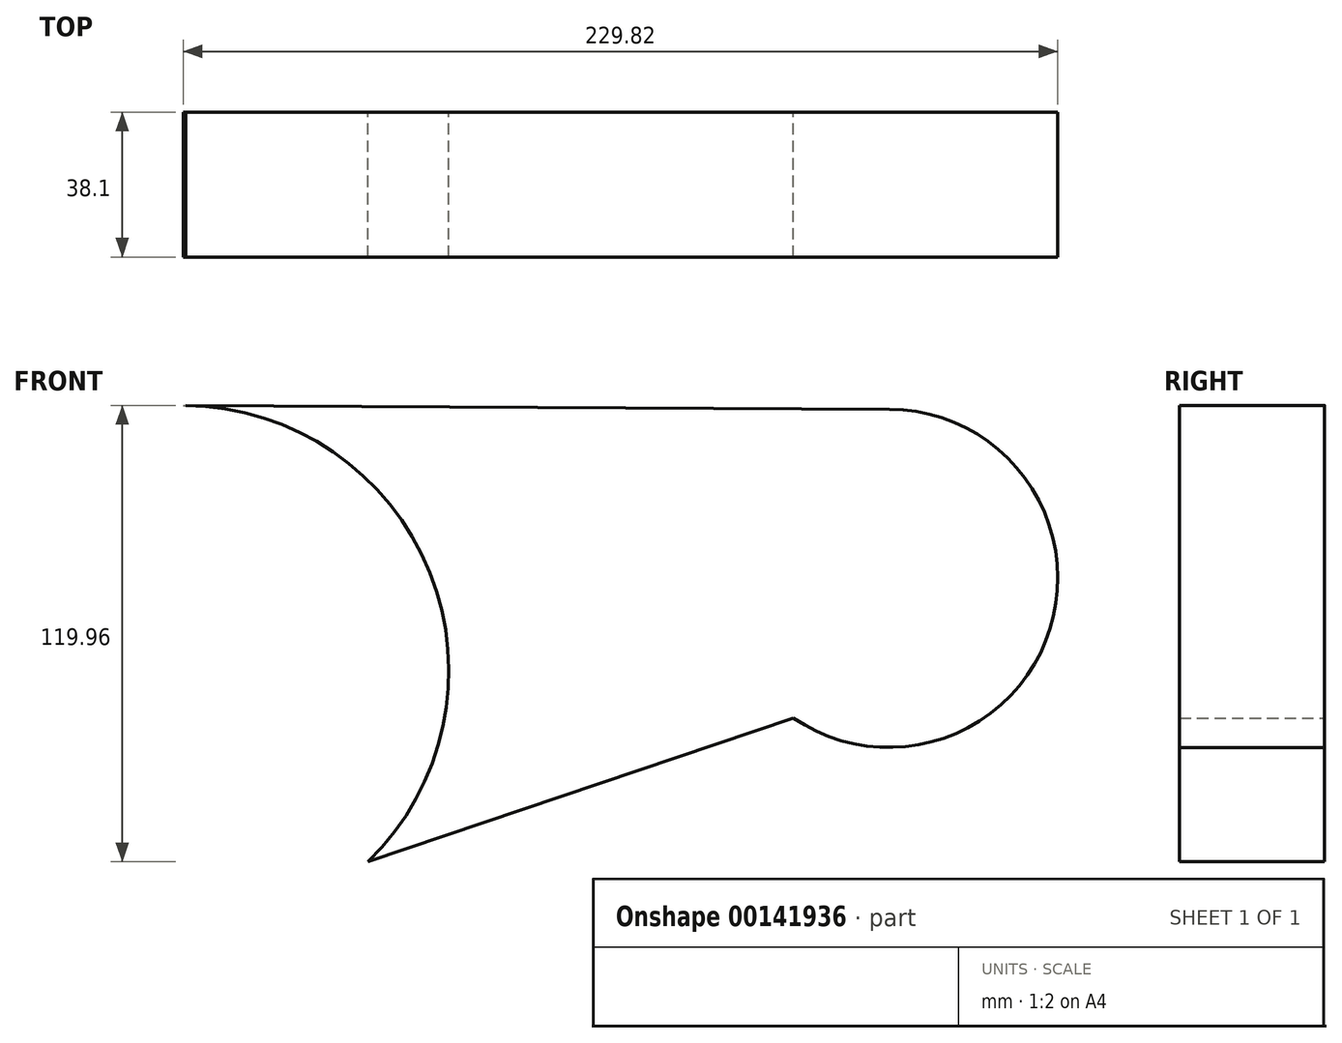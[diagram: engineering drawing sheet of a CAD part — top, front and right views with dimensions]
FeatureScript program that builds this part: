
annotation { "Feature Type Name" : "Feature", "Feature Type Description" : "" }
export const myFeature = defineFeature(function(context is Context, id is Id, definition is map)
    precondition{}
    {
        {
            var Q0;
            Q0=qCreatedBy(makeId("Front.planeOp"),FACE);
            var sketch = newSketch(context, id + "F0", { "sketchPlane" : qUnion([Q0])});
            skCircle(sketch, "E0", {"center": v(-118.41, -60.95) * mm, "radius": 69.85 * mm});
            skCircle(sketch, "E1", {"center": v(67.02, -36.54) * mm, "radius": 44.45 * mm});
            skLineSegment(sketch, "E2", {"start": v(-118.35, 8.9) * mm, "end": v(67.26, 7.91) * mm});
            skLineSegment(sketch, "E3", {"start": v(-69.75, -111.06) * mm, "end": v(41.97, -73.26) * mm});
            skSolve(sketch);
        }
        {
            var Q0;
            {var subQ0=sQuery(id+"F0.wireOp",EDGE,"E3");Q0=makeQuery(id+"F0.imprint","IMPRINT",FACE,{"disambiguationData":[TD([[makeQuery(id+"F0.imprint","IMPRINT",EDGE,{"derivedFrom":subQ0}),1.0]])]});}
            var Q1;
            {var subQ0=sQuery(id+"F0.wireOp",EDGE,"E2");var subQ1=sQuery(id+"F0.wireOp",EDGE,"E0");var subQ2=makeQuery(id+"F0.imprint","INTERSECT",VERTEX,{"disambiguationData":[OD(0.0)],"derivedFrom":[subQ1,subQ0]});Q1=makeQuery(id+"F0.imprint","IMPRINT",FACE,{"disambiguationData":[TD([[makeQuery(id+"F0.imprint","IMPRINT",EDGE,{"disambiguationData":[TD([[subQ2,-1.0]])],"derivedFrom":subQ1}),1.0]])]});}
            var Q2;
            {var subQ0=sQuery(id+"F0.wireOp",EDGE,"E1");var subQ1=makeQuery(id+"F0.imprint","INTERSECT",VERTEX,{"derivedFrom":[subQ0,sQuery(id+"F0.wireOp",EDGE,"E2")]});Q2=makeQuery(id+"F0.imprint","IMPRINT",FACE,{"disambiguationData":[TD([[makeQuery(id+"F0.imprint","IMPRINT",EDGE,{"disambiguationData":[TD([[subQ1,-1.0]])],"derivedFrom":subQ0}),1.0]])]});}
            extrude(context, id + "F1", {"entities" : qUnion([Q0, Q1, Q2]), "depth" : 38.1 * mm});
        }
    });
